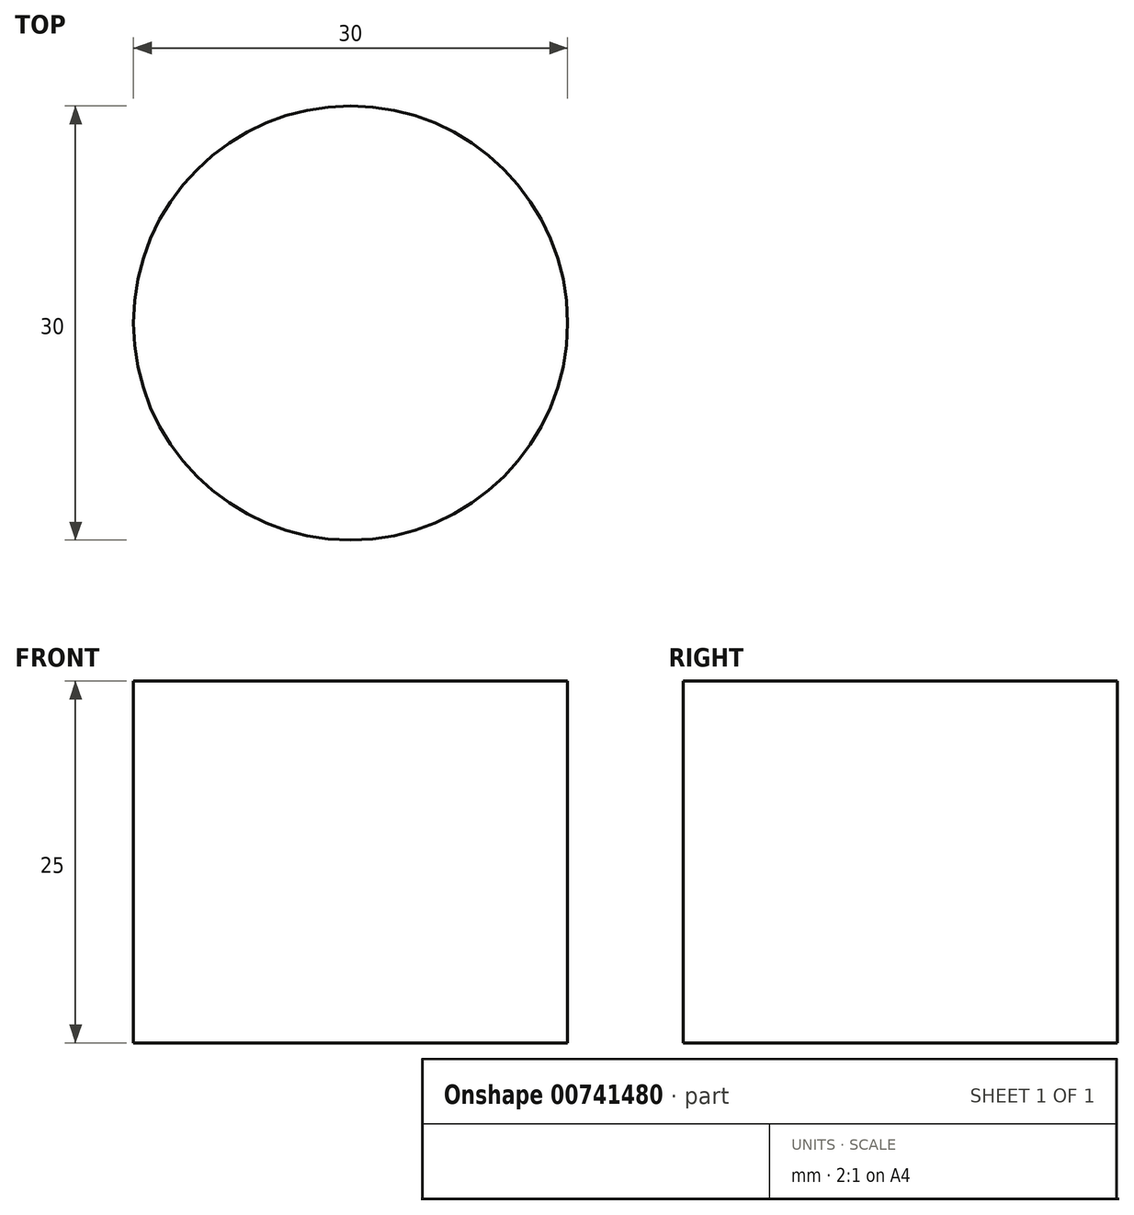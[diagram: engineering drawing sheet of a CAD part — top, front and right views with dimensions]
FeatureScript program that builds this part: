
annotation { "Feature Type Name" : "Feature", "Feature Type Description" : "" }
export const myFeature = defineFeature(function(context is Context, id is Id, definition is map)
    precondition{}
    {
        {
            var Q0;
            Q0=qCreatedBy(makeId("Top.planeOp"),FACE);
            var sketch = newSketch(context, id + "F0", { "sketchPlane" : qUnion([Q0])});
            skCircle(sketch, "E0", {"center": v(0, 0) * mm, "radius": 15 * mm});
            skSolve(sketch);
        }
        {
            var Q0;
            Q0 = qSketchRegion(id + "F0", true);
            extrude(context, id + "F1", {"entities" : qUnion([Q0]), "depth" : 25 * mm, "offsetDistance" : 25 * mm});
        }
    });
